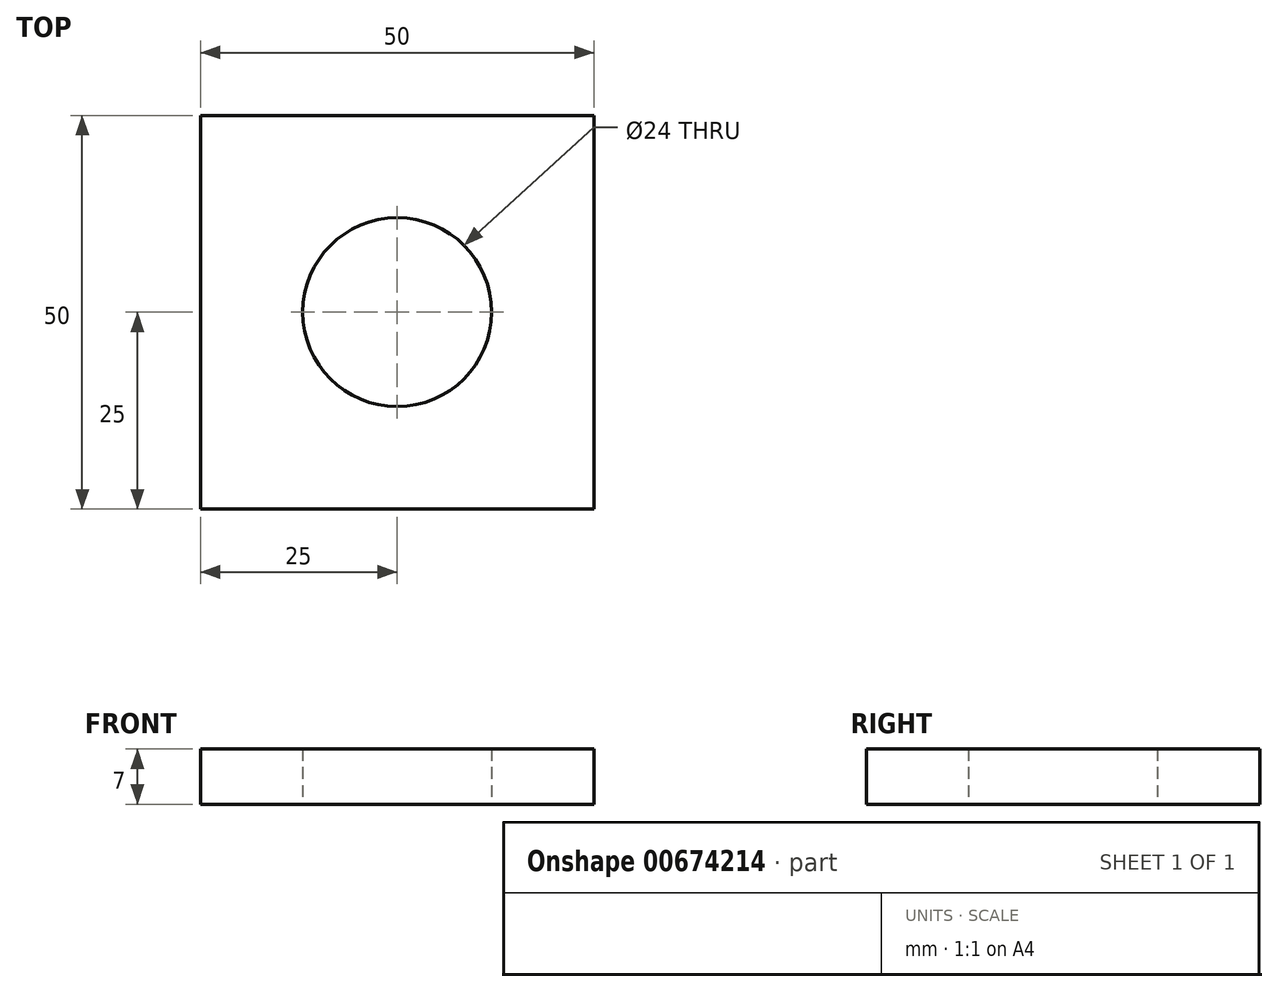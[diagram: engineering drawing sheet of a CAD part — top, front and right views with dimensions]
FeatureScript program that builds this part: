
annotation { "Feature Type Name" : "Feature", "Feature Type Description" : "" }
export const myFeature = defineFeature(function(context is Context, id is Id, definition is map)
    precondition{}
    {
        {
            var Q0;
            Q0=qCreatedBy(makeId("Top.planeOp"),FACE);
            var sketch = newSketch(context, id + "F0", { "sketchPlane" : qUnion([Q0])});
            skLineSegment(sketch, "E0.bottom", {"start": v(0, 0) * mm, "end": v(50, 0) * mm});
            skLineSegment(sketch, "E0.top", {"start": v(0, 50) * mm, "end": v(50, 50) * mm});
            skLineSegment(sketch, "E0.left", {"start": v(0, 0) * mm, "end": v(0, 50) * mm});
            skLineSegment(sketch, "E0.right", {"start": v(50, 0) * mm, "end": v(50, 20.5) * mm});
            skPoint(sketch, "E1.centerSnap0", {"position": v(0, 25) * mm});
            skLineSegment(sketch, "E2.trimOffspring", {"start": v(50, 44.5) * mm, "end": v(50, 50) * mm});
            skLineSegment(sketch, "E3", {"start": v(50, 44.5) * mm, "end": v(50, 20.5) * mm});
            skCircle(sketch, "E4", {"center": v(25, 25) * mm, "radius": 12 * mm});
            skPoint(sketch, "E4.centerSnap0", {"position": v(25, 0) * mm});
            skSolve(sketch);
        }
        {
            var Q0;
            Q0=makeQuery(id+"F0.imprint","IMPRINT",FACE,{"disambiguationData":[TD([[makeQuery(id+"F0.imprint","IMPRINT",EDGE,{"derivedFrom":sQuery(id+"F0.wireOp",EDGE,"E0.bottom")}),1.0]])]});
            extrude(context, id + "F1", {"entities" : qUnion([Q0]), "depth" : 7 * mm, "offsetDistance" : 25 * mm});
        }
    });
